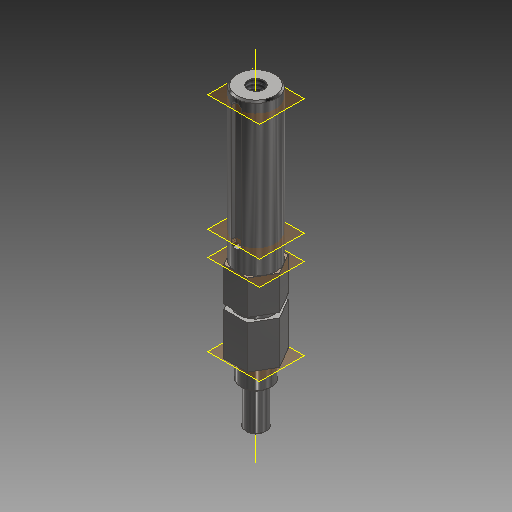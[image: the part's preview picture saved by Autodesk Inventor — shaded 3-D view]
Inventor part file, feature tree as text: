
AUTODESK INVENTOR PART (.ipt)
format: ipt  version: 2018 (Build 220112000, 112)  size: 168,448 bytes
history: native  units: in
note: dims shown in document units (in); Inventor stores cm internally (conversion verified against a paired STEP export)
features: plane x4, other x3, delete_face x1, hole x1, imported_body x1
ambient origin geometry x8: Origin, YZ Plane, XZ Plane, XY Plane, X Axis, Y Axis, Z Axis, Center Point
bodies: Body1 (feature_tree)
feature tree (10):
  other  "Toughbox_d03"
  other  "Toughbox_d03.ipt1"
  other  "Work Axis1"
  plane  "Work Plane1"
  plane  "Work Plane4"
  delete_face  "Delete Face1"
  hole  "Hole1"  [1 undecoded]
  imported_body  "Base1"
  plane  "Work Plane2"
  plane  "Work Plane3"
note: 1 required parameter value undecoded (feature->parameter linkage not recoverable at this tier; creation-order binding heuristic only, values carry confidence <= 0.55)
